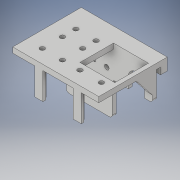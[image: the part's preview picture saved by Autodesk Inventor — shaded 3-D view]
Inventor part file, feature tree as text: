
AUTODESK INVENTOR PART (.ipt)
format: ipt  version: 2019 (Build 230136000, 136)  size: 268,288 bytes
history: native  units: mm
features: sketch x13, extrude x12, fillet x1, hole x1, plane x1
ambient origin geometry x8: Origin, YZ Plane, XZ Plane, XY Plane, X Axis, Y Axis, Z Axis, Center Point
bodies: Solid1 (feature_tree)
feature tree (28):
  extrude  "Extrusion1"  Depth=45.0mm
  extrude  "Extrusion2"  Depth=12.0mm
  fillet  "Fillet1"  Radius=12.0mm
  extrude  "Extrusion3"  Depth=12.0mm
  extrude  "Extrusion4"  Depth=30.0mm
  extrude  "Extrusion5"  Depth=13.0mm
  hole  "Hole1"  [1 undecoded]
  extrude  "Extrusion6"  Depth=25.0mm
  extrude  "Extrusion7"  Depth=2.0mm
  plane  "Work Plane1"
  extrude  "Extrusion8"  Depth=64.0mm
  extrude  "Extrusion9"  Depth=4.0mm
  extrude  "Extrusion10"  Depth=20.0mm
  extrude  "Extrusion12"  Depth=20.0mm
  extrude  "Extrusion13"  Depth=40.0mm TaperAngle=0.0deg
  sketch  "Sketch1"  dims[d0=64.0mm d1=45.0mm]
  sketch  "Sketch2"  dims[d2=12.0mm d3=12.0mm d4=12.0mm]
  sketch  "Sketch5"  dims[d5=12.0mm d6=3.5mm]
  sketch  "Sketch6"  dims[d7=30.0mm d8=14.0mm]
  sketch  "Sketch7"  dims[d9=3.5mm d10=13.0mm]
  sketch  "Sketch8"  dims[d11=33.0mm d12=3.0mm d13=0.0mm]
  sketch  "Sketch10"  dims[d14=30.0mm d15=25.0mm]
  sketch  "Sketch11"  dims[d16=3.0mm d17=0.0mm d18=2.0mm]
  sketch  "Sketch12"  dims[d20=11.0mm d21=64.0mm]
  sketch  "Sketch13"  dims[d22=4.0mm d23=0.0mm d24=4.0mm]
  sketch  "Sketch14"  dims[d25=40.0mm d26=0.0mm d27=20.0mm]
  sketch  "Sketch16"  dims[d28=3.0mm d29=20.0mm]
  sketch  "Sketch17"  dims[d30=26.0mm d31=40.0mm d32=0.0mm d33=10.0mm d34=10.0mm d35=5.0mm d36=5.0mm d37=5.0mm d38=8.0mm d39=8.0mm d40=5.0mm d41=3.5mm d42=6.0mm d43=5.0mm d44=1.5mm d45=90.0deg d46=8.0mm d47=20.594885mm d48=15.0mm d49=12.0mm d50=4.0mm d51=0.0mm d52=12.0mm d53=15.0mm d54=3.0mm d55=0.0mm d56=-20.0mm d57=3.0mm d58=0.0mm d59=5.0mm d60=5.0mm d61=0.0mm d63=15.0mm d64=2.0mm d65=2.5mm d66=6.0mm d67=2.5mm d68=6.0mm d70=2.0mm d72=16.5mm d73=13.0mm d74=20.0mm d75=0.0mm d86=26.0mm d87=5.0mm d88=10.0mm d89=0.0mm d90=10.0mm d91=0.0mm]
note: 1 required parameter value undecoded (feature->parameter linkage not recoverable at this tier; creation-order binding heuristic only, values carry confidence <= 0.55)
